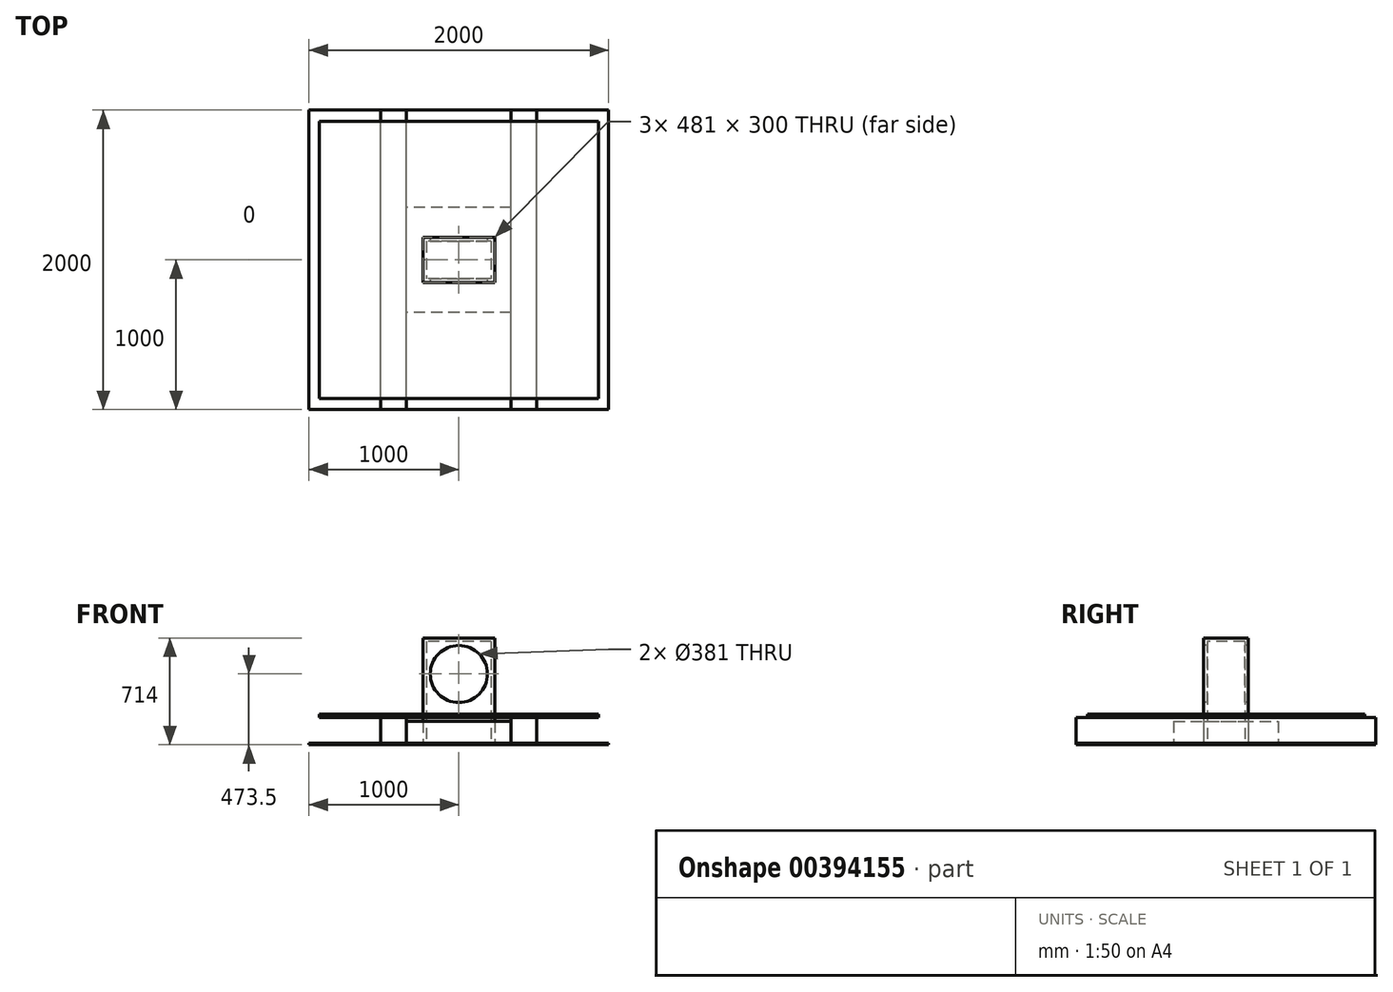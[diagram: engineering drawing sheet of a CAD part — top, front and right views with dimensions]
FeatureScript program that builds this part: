
annotation { "Feature Type Name" : "Feature", "Feature Type Description" : "" }
export const myFeature = defineFeature(function(context is Context, id is Id, definition is map)
    precondition{}
    {
        {
            var Q0;
            Q0=qCreatedBy(makeId("Front.planeOp"),FACE);
            var sketch = newSketch(context, id + "F0", { "sketchPlane" : qUnion([Q0])});
            skLineSegment(sketch, "E0.bottom", {"start": v(-520, 0) * mm, "end": v(-350, 0) * mm});
            skLineSegment(sketch, "E0.top", {"start": v(-520, 170) * mm, "end": v(-350, 170) * mm});
            skLineSegment(sketch, "E0.left", {"start": v(-520, 0) * mm, "end": v(-520, 170) * mm});
            skLineSegment(sketch, "E0.right", {"start": v(-350, 0) * mm, "end": v(-350, 170) * mm});
            skLineSegment(sketch, "E1.bottom", {"start": v(350, 0) * mm, "end": v(520, 0) * mm});
            skLineSegment(sketch, "E1.top", {"start": v(350, 170) * mm, "end": v(520, 170) * mm});
            skLineSegment(sketch, "E1.left", {"start": v(350, 0) * mm, "end": v(350, 170) * mm});
            skLineSegment(sketch, "E1.right", {"start": v(520, 0) * mm, "end": v(520, 170) * mm});
            skLineSegment(sketch, "E2", {"start": v(0, 0) * mm, "end": v(0, 677.87) * mm, "construction": true});
            skSolve(sketch);
        }
        {
            var Q0;
            Q0 = qSketchRegion(id + "F0", true);
            extrude(context, id + "F1", {"entities" : qUnion([Q0]), "endBound" : BoundingType.SYMMETRIC, "depth" : 2000 * mm});
        }
        {
            var Q0;
            Q0=qCreatedBy(makeId("Top.planeOp"),FACE);
            var sketch = newSketch(context, id + "F2", { "sketchPlane" : qUnion([Q0])});
            skLineSegment(sketch, "E3.bottom", {"start": v(1000, 1000) * mm, "end": v(-1000, 1000) * mm});
            skLineSegment(sketch, "E3.top", {"start": v(1000, -1000) * mm, "end": v(-1000, -1000) * mm});
            skLineSegment(sketch, "E3.left", {"start": v(1000, 1000) * mm, "end": v(1000, -1000) * mm});
            skLineSegment(sketch, "E3.right", {"start": v(-1000, 1000) * mm, "end": v(-1000, -1000) * mm});
            skPoint(sketch, "E3.middle", {"position": v(0, 0) * mm});
            skSolve(sketch);
        }
        {
            var Q0;
            Q0 = qSketchRegion(id + "F2", true);
            extrude(context, id + "F3", {"entities" : qUnion([Q0]), "oppositeDirection" : true, "depth" : 11 * mm});
        }
        {
            var Q0;
            Q0=makeQuery(id+"F3.opExtrude","CAP_FACE",FACE,{"disambiguationData":[OSD([sQuery(id+"F2.wireOp",EDGE,"E3.bottom"),sQuery(id+"F2.wireOp",EDGE,"E3.top"),sQuery(id+"F2.wireOp",EDGE,"E3.left"),sQuery(id+"F2.wireOp",EDGE,"E3.right")])],"isStart":false});
            var sketch = newSketch(context, id + "F4", { "sketchPlane" : qUnion([Q0])});
            skLineSegment(sketch, "E4.bottom", {"start": v(240.5, -150) * mm, "end": v(-240.5, -150) * mm});
            skLineSegment(sketch, "E4.top", {"start": v(240.5, 150) * mm, "end": v(-240.5, 150) * mm});
            skLineSegment(sketch, "E4.left", {"start": v(240.5, -150) * mm, "end": v(240.5, 150) * mm});
            skLineSegment(sketch, "E4.right", {"start": v(-240.5, -150) * mm, "end": v(-240.5, 150) * mm});
            skPoint(sketch, "E4.middle", {"position": v(0, 0) * mm});
            skSolve(sketch);
        }
        {
            var Q0;
            Q0 = qSketchRegion(id + "F4", true);
            extrude(context, id + "F5", {"entities" : qUnion([Q0]), "oppositeDirection" : true, "depth" : (20 * 25.4 + 11 + 170 + 25) * mm});
        }
        {
            var Q0;
            Q0=makeQuery(id+"F1.opExtrude","SWEPT_FACE",FACE,{"disambiguationData":[OSD([sQuery(id+"F0.wireOp",EDGE,"E0.top")])]});
            var sketch = newSketch(context, id + "F6", { "sketchPlane" : qUnion([Q0])});
            skLineSegment(sketch, "E5.bottom", {"start": v(931.64, -925.02) * mm, "end": v(-931.64, -925.02) * mm});
            skLineSegment(sketch, "E5.top", {"start": v(931.64, 925.02) * mm, "end": v(-931.64, 925.02) * mm});
            skLineSegment(sketch, "E5.left", {"start": v(931.64, -925.02) * mm, "end": v(931.64, 925.02) * mm});
            skLineSegment(sketch, "E5.right", {"start": v(-931.64, -925.02) * mm, "end": v(-931.64, 925.02) * mm});
            skPoint(sketch, "E5.middle", {"position": v(0, 0) * mm});
            skSolve(sketch);
        }
        {
            var Q0;
            Q0 = qSketchRegion(id + "F6", true);
            extrude(context, id + "F7", {"entities" : qUnion([Q0]), "depth" : 25 * mm});
        }
        {
            var Q0;
            Q0=makeQuery(id+"F5.opExtrude","SWEPT_BODY",BODY,{"disambiguationData":[OSD([sQuery(id+"F4.wireOp",EDGE,"E4.bottom"),sQuery(id+"F4.wireOp",EDGE,"E4.top"),sQuery(id+"F4.wireOp",EDGE,"E4.left"),sQuery(id+"F4.wireOp",EDGE,"E4.right")])]});
            var Q1;
            Q1=makeQuery(id+"F3.opExtrude","SWEPT_BODY",BODY,{"disambiguationData":[OSD([sQuery(id+"F2.wireOp",EDGE,"E3.bottom"),sQuery(id+"F2.wireOp",EDGE,"E3.top"),sQuery(id+"F2.wireOp",EDGE,"E3.left"),sQuery(id+"F2.wireOp",EDGE,"E3.right")])]});
            var Q2;
            Q2=makeQuery(id+"F7.opExtrude","SWEPT_BODY",BODY,{"disambiguationData":[OSD([sQuery(id+"F6.wireOp",EDGE,"E5.bottom"),sQuery(id+"F6.wireOp",EDGE,"E5.top"),sQuery(id+"F6.wireOp",EDGE,"E5.left"),sQuery(id+"F6.wireOp",EDGE,"E5.right")])]});
            booleanBodies(context, id + "F8", {"operationType" : BooleanOperationType.SUBTRACTION, "tools" : qUnion([Q0]), "targets" : qUnion([Q1, Q2]), "keepTools" : true});
        }
        {
            var Q0;
            Q0=makeQuery(id+"F5.opExtrude","CAP_FACE",FACE,{"disambiguationData":[OSD([sQuery(id+"F4.wireOp",EDGE,"E4.bottom"),sQuery(id+"F4.wireOp",EDGE,"E4.top"),sQuery(id+"F4.wireOp",EDGE,"E4.left"),sQuery(id+"F4.wireOp",EDGE,"E4.right")])],"isStart":true});
            shell(context, id + "F9", {"entities" : qUnion([Q0]), "thickness" : 25 * mm});
        }
        {
            var Q0;
            Q0=makeQuery(id+"F5.opExtrude","SWEPT_FACE",FACE,{"disambiguationData":[OSD([sQuery(id+"F4.wireOp",EDGE,"E4.top")])]});
            var sketch = newSketch(context, id + "F10", { "sketchPlane" : qUnion([Q0])});
            skCircle(sketch, "E6", {"center": v(0, 462.5) * mm, "radius": 190.5 * mm});
            skSolve(sketch);
        }
        {
            var Q0;
            Q0 = qSketchRegion(id + "F10", true);
            extrude(context, id + "F11", {"entities" : qUnion([Q0]), "operationType" : NewBodyOperationType.REMOVE, "endBound" : BoundingType.THROUGH_ALL, "oppositeDirection" : true, "depth" : 25 * mm});
        }
        {
            var Q0;
            Q0=makeQuery(id+"F3.opExtrude","CAP_FACE",FACE,{"disambiguationData":[OSD([sQuery(id+"F2.wireOp",EDGE,"E3.bottom"),sQuery(id+"F2.wireOp",EDGE,"E3.top"),sQuery(id+"F2.wireOp",EDGE,"E3.left"),sQuery(id+"F2.wireOp",EDGE,"E3.right")])],"isStart":true});
            var sketch = newSketch(context, id + "F12", { "sketchPlane" : qUnion([Q0])});
            skLineSegment(sketch, "E7.bottom", {"start": v(350, -350) * mm, "end": v(-350, -350) * mm});
            skLineSegment(sketch, "E7.top", {"start": v(350, 350) * mm, "end": v(-350, 350) * mm});
            skLineSegment(sketch, "E7.left", {"start": v(350, -350) * mm, "end": v(350, 350) * mm});
            skLineSegment(sketch, "E7.right", {"start": v(-350, -350) * mm, "end": v(-350, 350) * mm});
            skPoint(sketch, "E7.middle", {"position": v(0, 0) * mm});
            skLineSegment(sketch, "E8.0.0", {"start": v(240.5, -150) * mm, "end": v(240.5, 150) * mm});
            skLineSegment(sketch, "E8.0.1", {"start": v(240.5, 150) * mm, "end": v(-240.5, 150) * mm});
            skLineSegment(sketch, "E8.0.2", {"start": v(-240.5, 150) * mm, "end": v(-240.5, -150) * mm});
            skLineSegment(sketch, "E8.0.3", {"start": v(-240.5, -150) * mm, "end": v(240.5, -150) * mm});
            skSolve(sketch);
        }
        {
            var Q0;
            Q0 = qSketchRegion(id + "F12", true);
            extrude(context, id + "F13", {"entities" : qUnion([Q0]), "depth" : 145 * mm});
        }
    });
